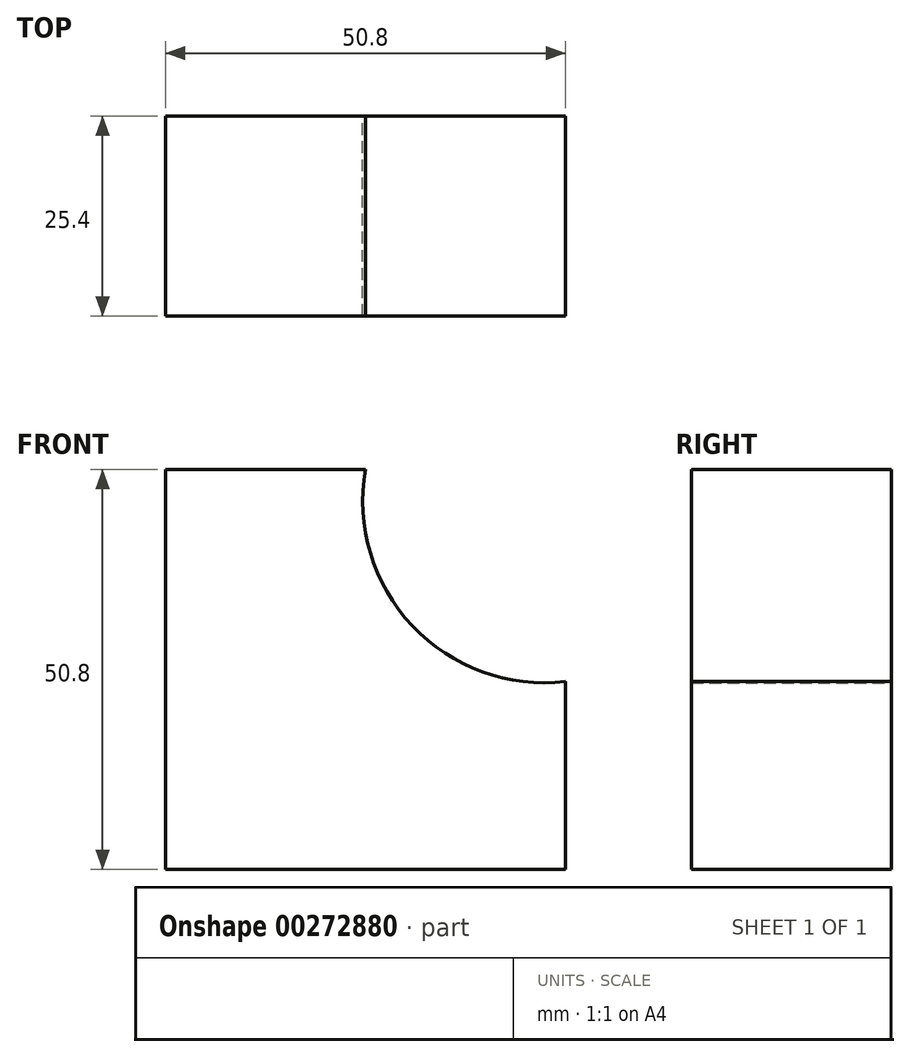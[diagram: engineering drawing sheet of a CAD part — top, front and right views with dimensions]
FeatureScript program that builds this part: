
annotation { "Feature Type Name" : "Feature", "Feature Type Description" : "" }
export const myFeature = defineFeature(function(context is Context, id is Id, definition is map)
    precondition{}
    {
        {
            var Q0;
            Q0=qCreatedBy(makeId("Front.planeOp"),FACE);
            var sketch = newSketch(context, id + "F0", { "sketchPlane" : qUnion([Q0])});
            skLineSegment(sketch, "E0", {"start": v(0, 0) * mm, "end": v(-50.8, 0) * mm});
            skLineSegment(sketch, "E1", {"start": v(-50.8, 0) * mm, "end": v(-50.8, 50.8) * mm});
            skLineSegment(sketch, "E2", {"start": v(-50.8, 50.8) * mm, "end": v(-25.4, 50.8) * mm});
            skArc(sketch, "E3", {"start": v(-25.4, 50.8) * mm, "mid": v(-19.46, 30.96) * mm, "end": v(0, 23.87) * mm});
            skLineSegment(sketch, "E4", {"start": v(0, 23.87) * mm, "end": v(0, -5.35) * mm});
            skSolve(sketch);
        }
        {
            var Q0;
            Q0 = qSketchRegion(id + "F0", true);
            extrude(context, id + "F1", {"entities" : qUnion([Q0]), "depth" : 25.4 * mm});
        }
    });
